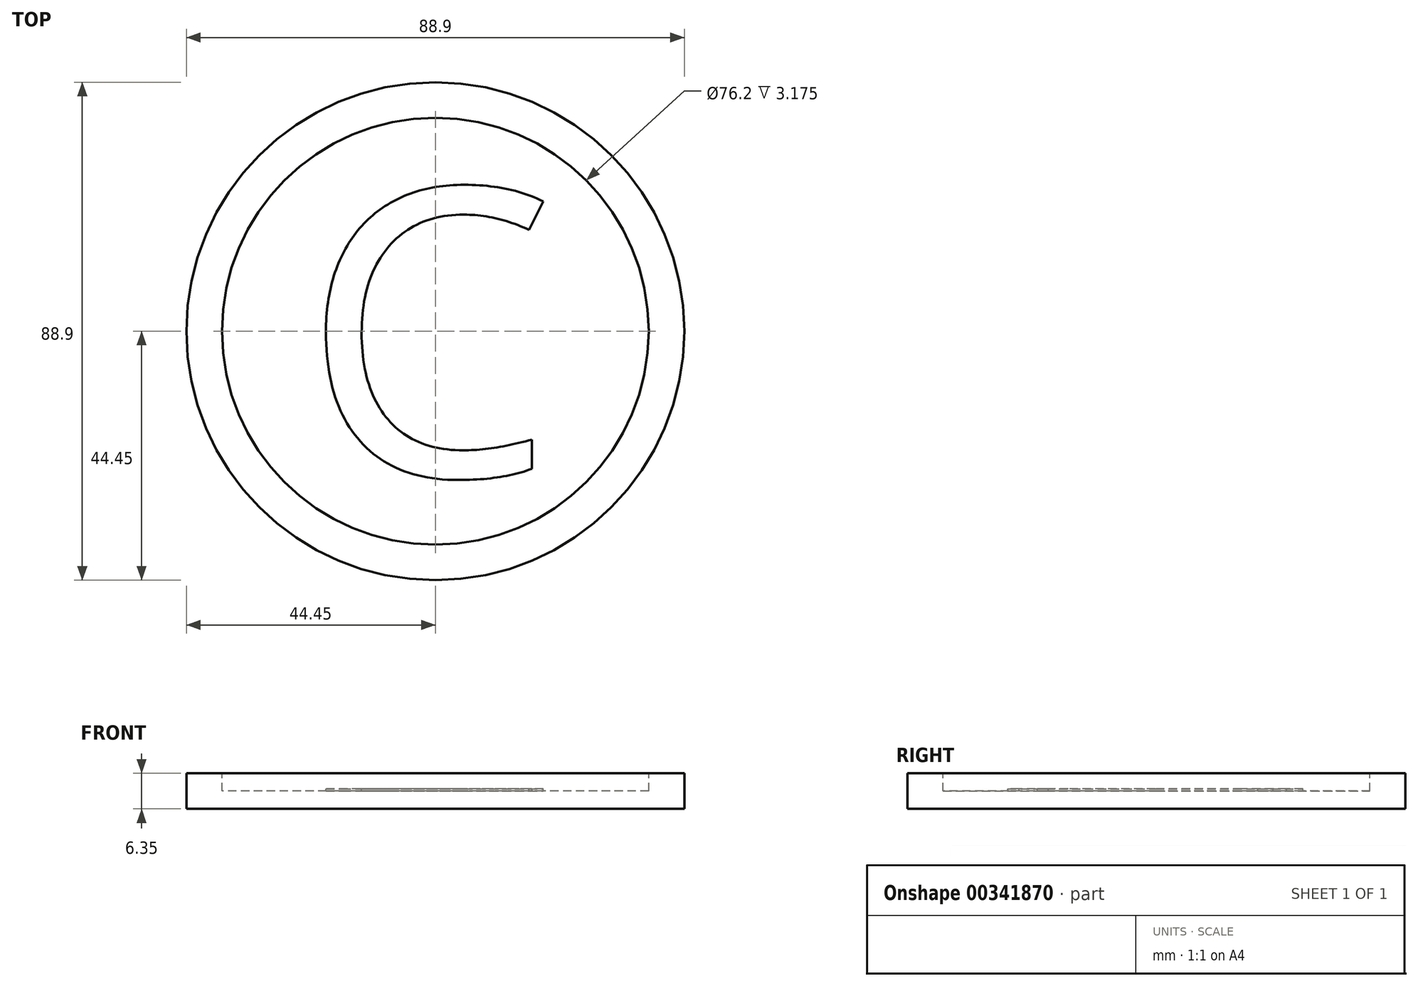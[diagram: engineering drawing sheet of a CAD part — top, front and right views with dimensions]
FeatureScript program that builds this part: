
annotation { "Feature Type Name" : "Feature", "Feature Type Description" : "" }
export const myFeature = defineFeature(function(context is Context, id is Id, definition is map)
    precondition{}
    {
        {
            var Q0;
            Q0=qCreatedBy(makeId("Top.planeOp"),FACE);
            var sketch = newSketch(context, id + "F0", { "sketchPlane" : qUnion([Q0])});
            skCircle(sketch, "E0", {"center": v(0, 0) * mm, "radius": 44.45 * mm});
            skSolve(sketch);
        }
        {
            var Q0;
            Q0=makeQuery(id+"F0.imprint","IMPRINT",FACE,{"disambiguationData":[TD([[makeQuery(id+"F0.imprint","IMPRINT",EDGE,{"derivedFrom":sQuery(id+"F0.wireOp",EDGE,"E0")}),1.0]])]});
            extrude(context, id + "F1", {"entities" : qUnion([Q0]), "depth" : 6.35 * mm});
        }
        {
            var Q0;
            Q0=makeQuery(id+"F1.opExtrude","CAP_FACE",FACE,{"disambiguationData":[OSD([sQuery(id+"F0.wireOp",EDGE,"E0")])],"isStart":false});
            cPlane(context, id + "F2", {"entities" : qUnion([Q0]), "cplaneType" : CPlaneType.OFFSET, "offset" : 0 * mm, "width" : 152.4 * mm, "height" : 152.4 * mm});
        }
        {
            var Q0;
            Q0=qCreatedBy(id+"F2.planeOp",FACE);
            var sketch = newSketch(context, id + "F3", { "sketchPlane" : qUnion([Q0])});
            skCircle(sketch, "E1", {"center": v(0, 0) * mm, "radius": 38.1 * mm});
            skPoint(sketch, "E2", {"position": v(-23.92, -8.08) * mm});
            skPoint(sketch, "E3", {"position": v(-23.92, -25.86) * mm});
            skPoint(sketch, "E4", {"position": v(0, -25.86) * mm});
            skText(sketch, "E5", { "text": "C", "fontName": "OpenSans-Regular.ttf"});
            const initialGuessF3  = {"E5": [-0.02392, -0.02586, 1, 0, 0.05172]};
            skSetInitialGuess(sketch, initialGuessF3);
            skSolve(sketch);
        }
        {
            var Q0;
            Q0=makeQuery(id+"F3.imprint","IMPRINT",FACE,{"disambiguationData":[TD([[makeQuery(id+"F3.imprint","IMPRINT",EDGE,{"derivedFrom":sQuery(id+"F3.wireOp",EDGE,"E1")}),1.0]])]});
            extrude(context, id + "F4", {"entities" : qUnion([Q0]), "operationType" : NewBodyOperationType.REMOVE, "oppositeDirection" : true, "depth" : 3.17 * mm});
        }
        {
            var Q0;
            Q0=makeQuery(id+"F3.imprint","IMPRINT",FACE,{"disambiguationData":[TD([[makeQuery(id+"F3.imprint","IMPRINT",EDGE,{"derivedFrom":sQuery(id+"F3.wireOp",EDGE,"E5.sketch_text.stroke-0")}),-1.0]])]});
            extrude(context, id + "F5", {"entities" : qUnion([Q0]), "operationType" : NewBodyOperationType.REMOVE, "oppositeDirection" : true, "depth" : 2.8 * mm});
        }
    });
